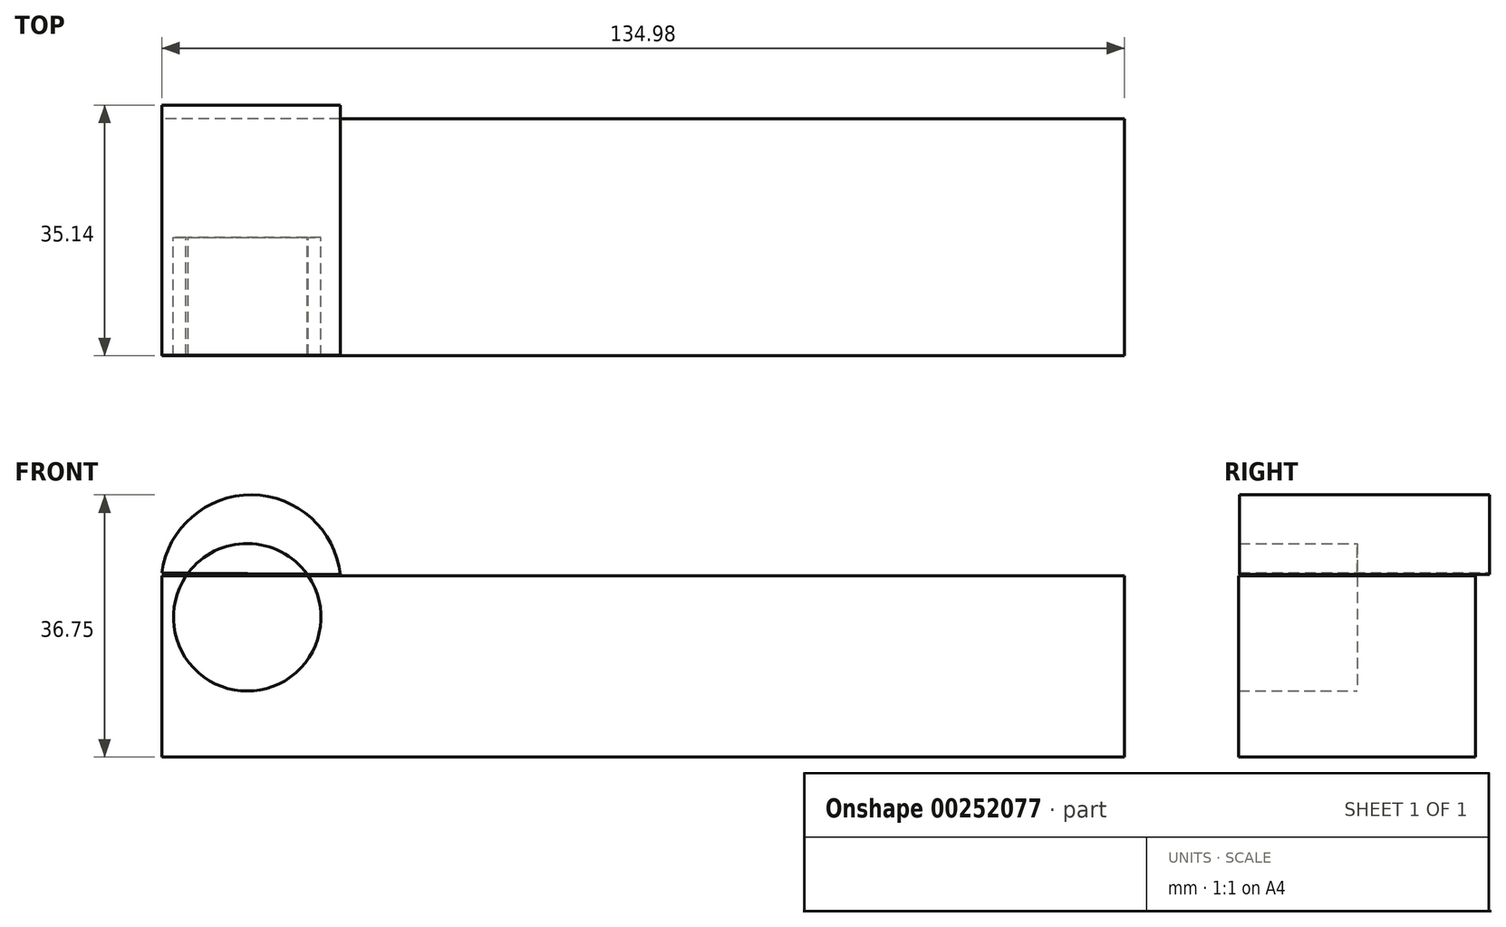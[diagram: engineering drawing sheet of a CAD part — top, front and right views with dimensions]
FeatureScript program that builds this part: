
annotation { "Feature Type Name" : "Feature", "Feature Type Description" : "" }
export const myFeature = defineFeature(function(context is Context, id is Id, definition is map)
    precondition{}
    {
        {
            var Q0;
            Q0=qCreatedBy(makeId("Top.planeOp"),FACE);
            var sketch = newSketch(context, id + "F0", { "sketchPlane" : qUnion([Q0])});
            skLineSegment(sketch, "E0.bottom", {"start": v(67.5, -16.6) * mm, "end": v(-67.5, -16.6) * mm});
            skLineSegment(sketch, "E0.top", {"start": v(67.5, 16.6) * mm, "end": v(-67.5, 16.6) * mm});
            skLineSegment(sketch, "E0.left", {"start": v(67.5, -16.6) * mm, "end": v(67.5, 16.6) * mm});
            skLineSegment(sketch, "E0.right", {"start": v(-67.5, -16.6) * mm, "end": v(-67.5, 16.6) * mm});
            skPoint(sketch, "E0.middle", {"position": v(0, 0) * mm});
            skSolve(sketch);
        }
        {
            var Q0;
            Q0=makeQuery(id+"F0.imprint","IMPRINT",FACE,{"disambiguationData":[TD([[makeQuery(id+"F0.imprint","IMPRINT",EDGE,{"derivedFrom":sQuery(id+"F0.wireOp",EDGE,"E0.bottom")}),-1.0]])]});
            extrude(context, id + "F1", {"entities" : qUnion([Q0]), "depth" : 25.4 * mm});
        }
        {
            var Q0;
            Q0=qCreatedBy(makeId("Front.planeOp"),FACE);
            var sketch = newSketch(context, id + "F2", { "sketchPlane" : qUnion([Q0])});
            skArc(sketch, "E1", {"start": v(-42.45, 25.58) * mm, "mid": v(-54.85, 36.75) * mm, "end": v(-67.5, 25.85) * mm});
            skLineSegment(sketch, "E2", {"start": v(-67.5, 25.85) * mm, "end": v(-42.45, 25.58) * mm});
            skSolve(sketch);
        }
        {
            var Q0;
            Q0=makeQuery(id+"F2.imprint","IMPRINT",FACE,{"disambiguationData":[TD([[makeQuery(id+"F2.imprint","IMPRINT",EDGE,{"derivedFrom":sQuery(id+"F2.wireOp",EDGE,"E1")}),1.0]])]});
            extrude(context, id + "F3", {"entities" : qUnion([Q0]), "depth" : 16.5 * mm});
        }
        {
            var Q0;
            Q0=makeQuery(id+"F3.opExtrude","CAP_FACE",FACE,{"disambiguationData":[OSD([sQuery(id+"F2.wireOp",EDGE,"E1"),sQuery(id+"F2.wireOp",EDGE,"E2")])],"isStart":true});
            extrude(context, id + "F4", {"entities" : qUnion([Q0]), "operationType" : NewBodyOperationType.ADD, "depth" : 18.54 * mm});
        }
        {
            var Q0;
            Q0=qCreatedBy(makeId("Front.planeOp"),FACE);
            var sketch = newSketch(context, id + "F5", { "sketchPlane" : qUnion([Q0])});
            skCircle(sketch, "E3", {"center": v(-55.52, 19.6) * mm, "radius": 10.34 * mm});
            skSolve(sketch);
        }
        {
            var Q0;
            Q0 = qSketchRegion(id + "F5", true);
            extrude(context, id + "F6", {"entities" : qUnion([Q0]), "operationType" : NewBodyOperationType.REMOVE, "depth" : 81.03 * mm});
        }
    });
